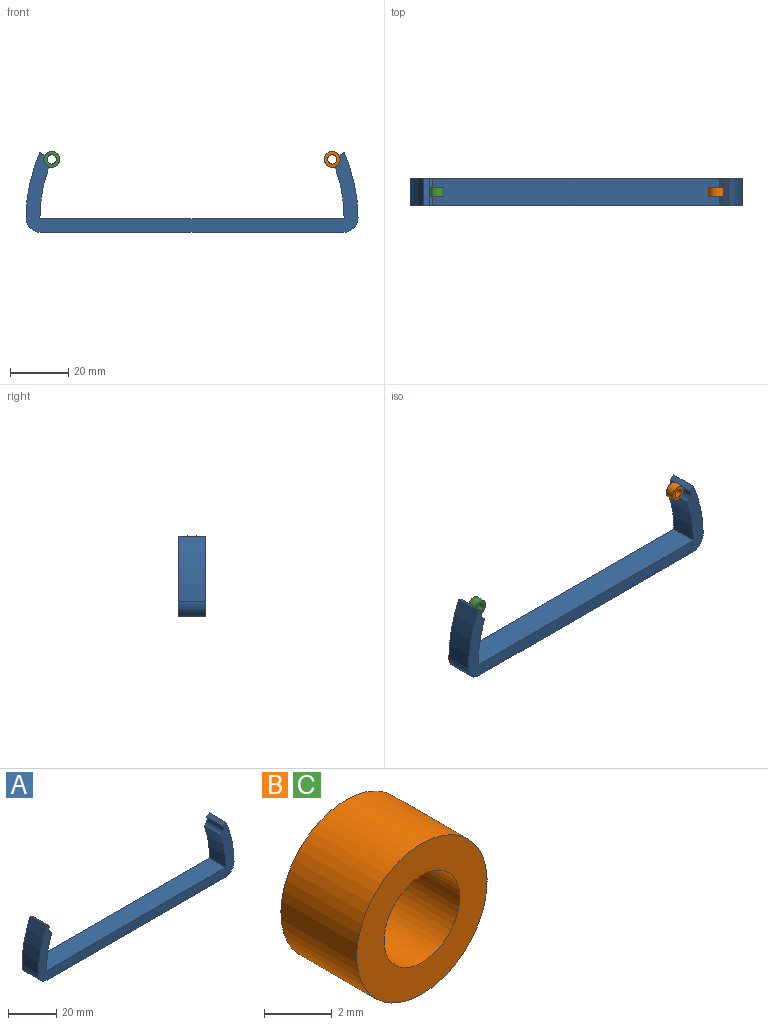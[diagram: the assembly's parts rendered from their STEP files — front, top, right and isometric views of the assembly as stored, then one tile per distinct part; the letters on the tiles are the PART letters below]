
ASSEMBLY  parts=3 mates=2
PART A: 14 faces, bbox 114.3x9.5x27.6 mm
  f0: cylinder r=2.73mm len=9.53mm, axis (0,1,0), area 45.1mm2, adj f1,f9,f10,f11
  f1: plane 9.53x1.78mm, normal (0.51,0,0.86), area 19.8mm2, adj f0,f2,f10,f11
  f2: cylinder r=57.15mm len=22.49mm, axis (0,1,0), area 220.5mm2, adj f1,f10,f11,f12
  f3: plane 104.14x9.53mm, normal (0,0,-1), area 991.9mm2, adj f10,f11,f12,f13
  f4: cylinder r=57.15mm len=22.49mm, axis (0,1,0), area 220.5mm2, adj f5,f10,f11,f13
  f5: plane 9.53x1.78mm, normal (-0.51,0,0.86), area 19.8mm2, adj f4,f6,f10,f11
  f6: cylinder r=2.73mm len=9.53mm, axis (0,1,0), area 45.1mm2, adj f5,f7,f10,f11
  f7: cylinder r=52.39mm len=17.84mm, axis (0,1,0), area 173.4mm2, adj f6,f8,f10,f11
  f8: plane 104.78x9.53mm, normal (0,0,1), area 998mm2, adj f7,f9,f10,f11
  f9: cylinder r=52.39mm len=17.84mm, axis (0,1,0), area 173.4mm2, adj f0,f8,f10,f11
  f10: plane 114.3x27.6mm, normal (0,-1,0), area 732mm2, adj f0,f1,f2,f3,f4,f5,f6,f7
  f11: plane 114.3x27.6mm, normal (0,1,0), area 732mm2, adj f0,f1,f2,f3,f4,f5,f6,f7
  f12: cylinder r=5.08mm len=9.53mm, axis (0,1,0), area 76.3mm2, adj f2,f3,f10,f11
  f13: cylinder r=5.08mm len=9.53mm, axis (0,1,0), area 76.3mm2, adj f3,f4,f10,f11
PART B: 4 faces, bbox 5.5x3.2x5.5 mm
  f0: cylinder r=1.59mm len=3.18mm, axis (0,1,0), area 31.7mm2, adj f2,f3
  f1: cylinder r=2.73mm len=5.46mm, axis (0,1,0), area 54.5mm2, adj f2,f3
  f2: plane 5.46x5.46mm, normal (0,-1,0), area 15.5mm2, adj f0,f1
  f3: plane 5.46x5.46mm, normal (0,1,0), area 15.5mm2, adj f0,f1
PART C: same geometry as B
PLACE A t=(4.84,37.66,-2.93)mm
PLACE B t=(53.1,34.49,22.21)mm
PLACE C t=(-43.42,34.49,22.21)mm
MATE fastened C.f0 <-> A.f0  axis (0,1,0) through (-43.42,32.9,22.21)mm
MATE fastened B.f0 <-> A.f6  axis (0,1,0) through (53.1,32.9,22.21)mm
